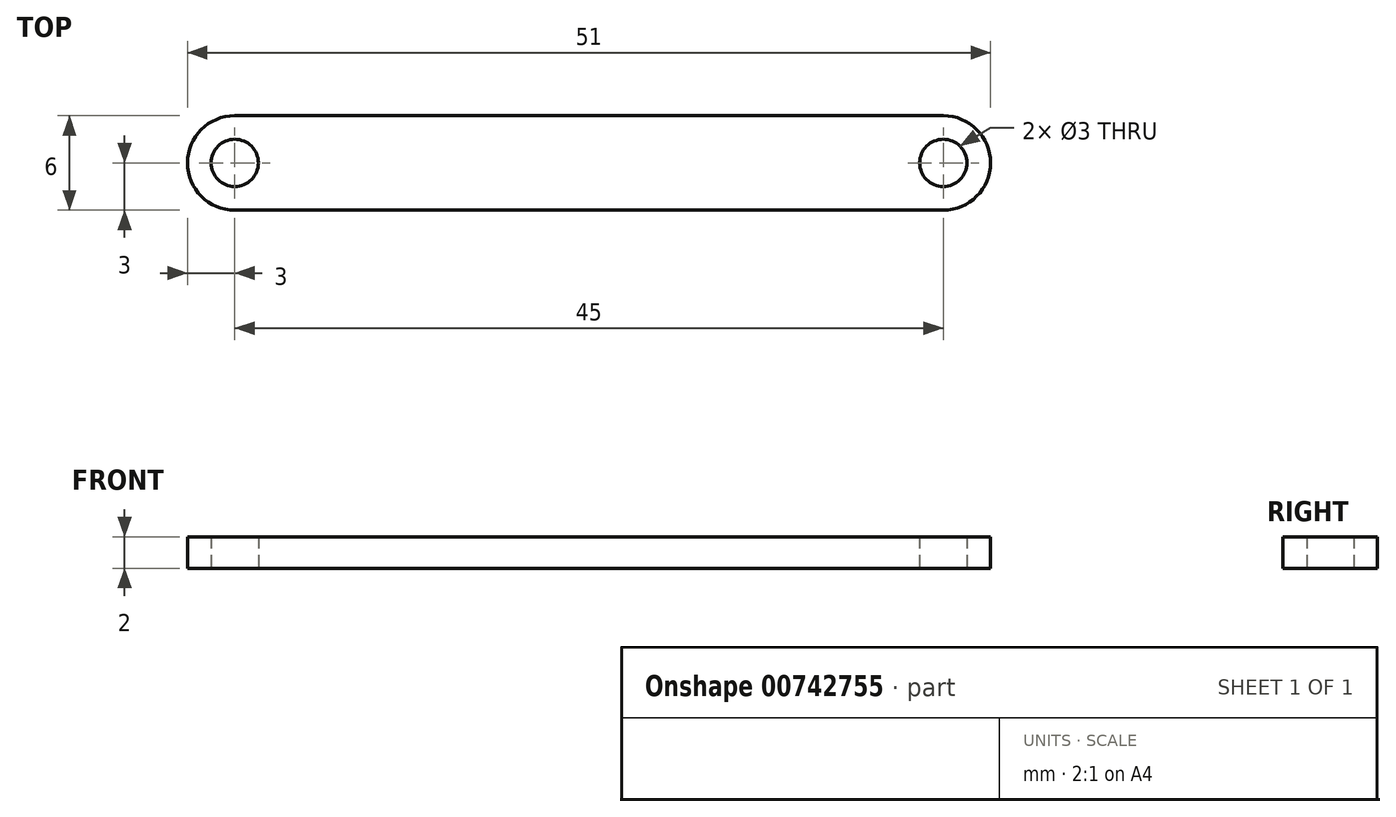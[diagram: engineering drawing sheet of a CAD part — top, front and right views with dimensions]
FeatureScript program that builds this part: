
annotation { "Feature Type Name" : "Feature", "Feature Type Description" : "" }
export const myFeature = defineFeature(function(context is Context, id is Id, definition is map)
    precondition{}
    {
        {
            var Q0;
            Q0=qCreatedBy(makeId("Top.planeOp"),FACE);
            var sketch = newSketch(context, id + "F0", { "sketchPlane" : qUnion([Q0])});
            skLineSegment(sketch, "E0.bottom", {"start": v(22.5, -3) * mm, "end": v(-22.5, -3) * mm});
            skLineSegment(sketch, "E0.top", {"start": v(22.5, 3) * mm, "end": v(-22.5, 3) * mm});
            skPoint(sketch, "E0.middle", {"position": v(0, 0) * mm});
            skArc(sketch, "E1", {"start": v(-22.5, 3) * mm, "mid": v(-25.5, 0) * mm, "end": v(-22.5, -3) * mm});
            skArc(sketch, "E2", {"start": v(22.5, -3) * mm, "mid": v(25.5, 0) * mm, "end": v(22.5, 3) * mm});
            skCircle(sketch, "E3", {"center": v(-22.5, 0) * mm, "radius": 1.5 * mm});
            skCircle(sketch, "E4", {"center": v(22.5, 0) * mm, "radius": 1.5 * mm});
            skSolve(sketch);
        }
        {
            var Q0;
            Q0 = qSketchRegion(id + "F0", true);
            extrude(context, id + "F1", {"entities" : qUnion([Q0]), "depth" : 2 * mm, "offsetDistance" : 25 * mm});
        }
    });
